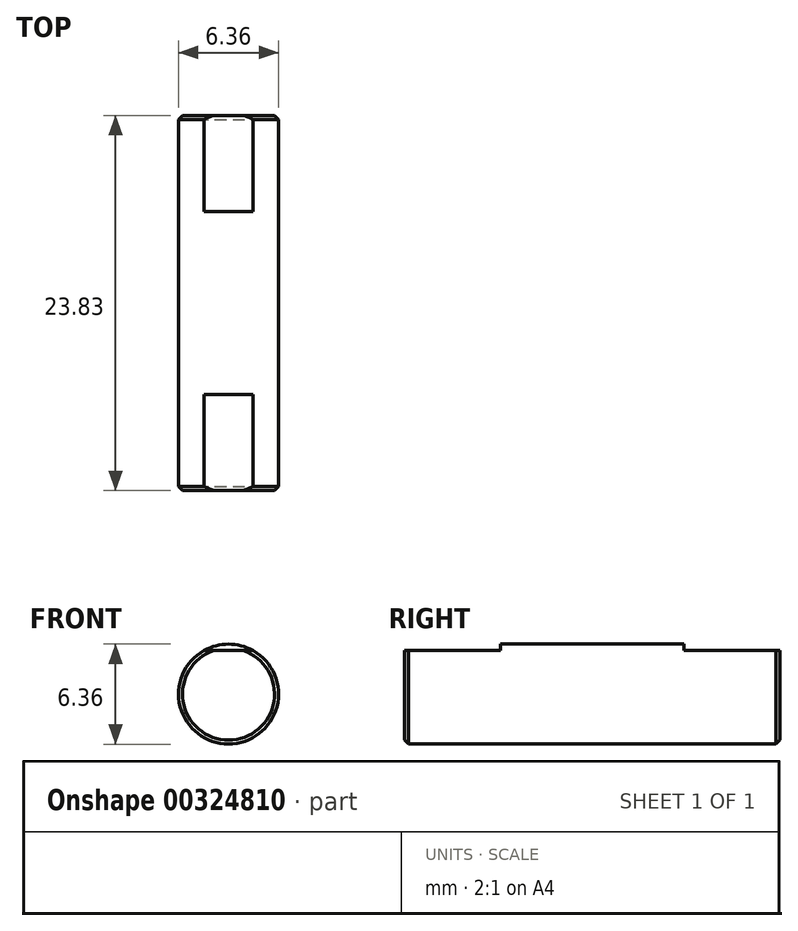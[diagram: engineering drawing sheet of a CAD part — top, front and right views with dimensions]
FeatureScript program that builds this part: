
annotation { "Feature Type Name" : "Feature", "Feature Type Description" : "" }
export const myFeature = defineFeature(function(context is Context, id is Id, definition is map)
    precondition{}
    {
        {
            var Q0;
            Q0=qCreatedBy(makeId("Front.planeOp"),FACE);
            var sketch = newSketch(context, id + "F0", { "sketchPlane" : qUnion([Q0])});
            skCircle(sketch, "E0", {"center": v(0, 0) * mm, "radius": 3.18 * mm});
            skSolve(sketch);
        }
        {
            var Q0;
            Q0=makeQuery(id+"F0.imprint","IMPRINT",FACE,{"disambiguationData":[TD([[makeQuery(id+"F0.imprint","IMPRINT",EDGE,{"derivedFrom":sQuery(id+"F0.wireOp",EDGE,"E0")}),1.0]])]});
            extrude(context, id + "F1", {"entities" : qUnion([Q0]), "depth" : 23.83 * mm, "offsetDistance" : 25.4 * mm});
        }
        {
            var Q0;
            Q0=makeQuery(id+"F1.opExtrude","CAP_FACE",FACE,{"disambiguationData":[OSD([sQuery(id+"F0.wireOp",EDGE,"E0")])],"isStart":false});
            var sketch = newSketch(context, id + "F2", { "sketchPlane" : qUnion([Q0])});
            skLineSegment(sketch, "E1", {"start": v(-1.55, 2.77) * mm, "end": v(1.55, 2.77) * mm});
            skArc(sketch, "E2", {"start": v(-1.55, 2.77) * mm, "mid": v(0, 3.18) * mm, "end": v(1.55, 2.77) * mm});
            skSolve(sketch);
        }
        {
            var Q0;
            Q0=makeQuery(id+"F2.imprint","IMPRINT",FACE,{"disambiguationData":[TD([[makeQuery(id+"F2.imprint","IMPRINT",EDGE,{"derivedFrom":sQuery(id+"F2.wireOp",EDGE,"E1")}),1.0]])]});
            extrude(context, id + "F3", {"entities" : qUnion([Q0]), "operationType" : NewBodyOperationType.REMOVE, "oppositeDirection" : true, "depth" : 6.1 * mm, "offsetDistance" : 25.4 * mm});
        }
        {
            var Q0;
            Q0=makeQuery(id+"F1.opExtrude","CAP_FACE",FACE,{"disambiguationData":[OSD([sQuery(id+"F0.wireOp",EDGE,"E0")])],"isStart":true});
            var sketch = newSketch(context, id + "F4", { "sketchPlane" : qUnion([Q0])});
            skLineSegment(sketch, "E3", {"start": v(-1.55, 2.77) * mm, "end": v(1.55, 2.77) * mm});
            skArc(sketch, "E4", {"start": v(-1.55, 2.77) * mm, "mid": v(0, 3.18) * mm, "end": v(1.55, 2.77) * mm});
            skSolve(sketch);
        }
        {
            var Q0;
            Q0=makeQuery(id+"F4.imprint","IMPRINT",FACE,{"disambiguationData":[TD([[makeQuery(id+"F4.imprint","IMPRINT",EDGE,{"derivedFrom":sQuery(id+"F4.wireOp",EDGE,"E3")}),1.0]])]});
            extrude(context, id + "F5", {"entities" : qUnion([Q0]), "operationType" : NewBodyOperationType.REMOVE, "oppositeDirection" : true, "depth" : 6.1 * mm, "offsetDistance" : 25.4 * mm});
        }
        {
            var Q0;
            Q0=makeQuery(id+"F1.opExtrude","CAP_EDGE",EDGE,{"disambiguationData":[OSD([sQuery(id+"F0.wireOp",EDGE,"E0")])],"isStart":true});
            var Q1;
            Q1=makeQuery(id+"F1.opExtrude","CAP_EDGE",EDGE,{"disambiguationData":[OSD([sQuery(id+"F0.wireOp",EDGE,"E0")])],"isStart":false});
            chamfer(context, id + "F6", {"entities" : qUnion([Q0, Q1]), "width" : 0.25 * mm, "tangentPropagation" : true});
        }
    });
